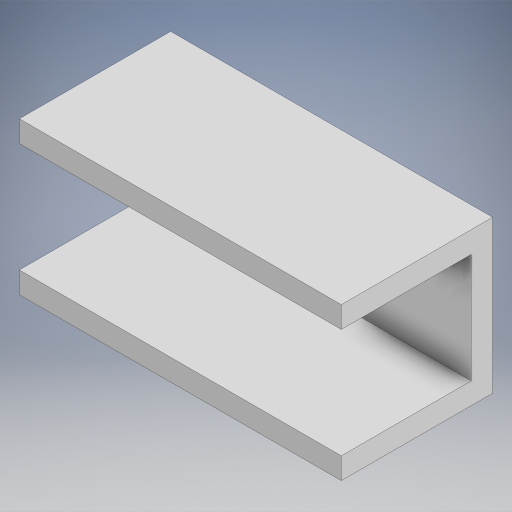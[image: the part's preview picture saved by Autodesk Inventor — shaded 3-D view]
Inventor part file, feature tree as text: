
AUTODESK INVENTOR PART (.ipt)
format: ipt  version: 2024.2 (Build 282272000, 272)  size: 193,536 bytes
history: native  units: in
note: dims shown in document units (in); Inventor stores cm internally (conversion verified against a paired STEP export)
features: extrude x1, sketch x1
ambient origin geometry x8: Origin, YZ Plane, XZ Plane, XY Plane, X Axis, Y Axis, Z Axis, Center Point
bodies: Solid1 (feature_tree)
feature tree (2):
  extrude  "Extrusion1"  [1 undecoded]
  sketch  "Sketch1"  dims[d6=3.0in d7=0.0in]
note: 1 required parameter value undecoded (feature->parameter linkage not recoverable at this tier; creation-order binding heuristic only, values carry confidence <= 0.55)
